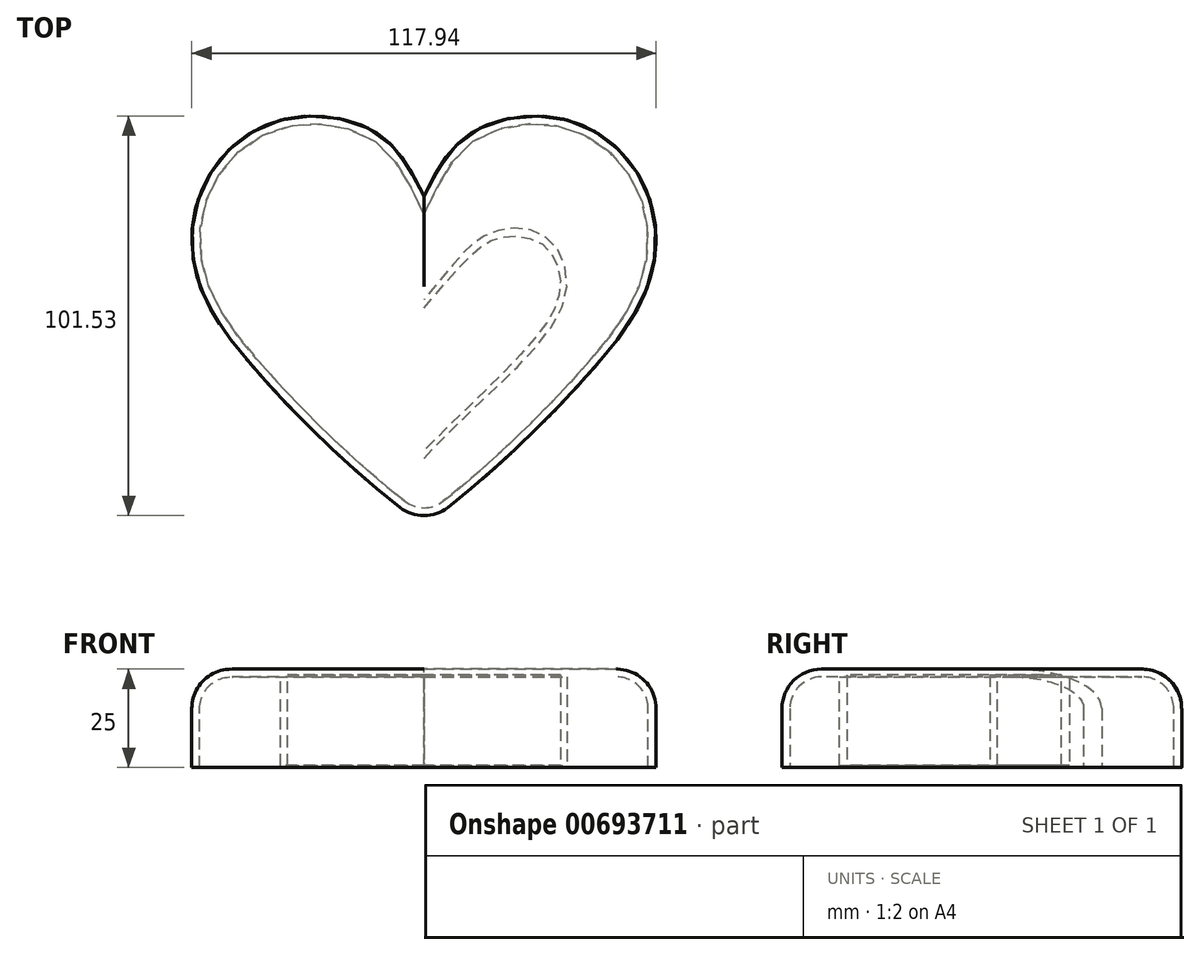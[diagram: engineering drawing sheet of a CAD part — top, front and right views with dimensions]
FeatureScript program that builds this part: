
annotation { "Feature Type Name" : "Feature", "Feature Type Description" : "" }
export const myFeature = defineFeature(function(context is Context, id is Id, definition is map)
    precondition{}
    {
        {
            var Q0;
            Q0=qCreatedBy(makeId("Top.planeOp"),FACE);
            var sketch = newSketch(context, id + "F0", { "sketchPlane" : qUnion([Q0])});
            skLineSegment(sketch, "E0", {"start": v(0, 39.92) * mm, "end": v(0, -43.63) * mm, "construction": true});
            skFitSpline(sketch, "E1", {"points": [v(0, 39.92) * mm, v(14.39, 57.24) * mm, v(36.67, 59.1) * mm, v(54, 46.1) * mm, v(58.95, 27.54) * mm, v(53.69, 10.21) * mm, v(41.3, -5.88) * mm, v(25.84, -21.97) * mm, v(0, -43.63) * mm], "startDerivative": vector(107.36, 222.12) * mm, "endDerivative": vector(-154.66, -101.42) * mm});
            skFitSpline(sketch, "E2.MirrorCS", {"points": [v(0, 39.92) * mm, v(-14.39, 57.24) * mm, v(-36.67, 59.1) * mm, v(-54, 46.1) * mm, v(-58.95, 27.54) * mm, v(-53.69, 10.21) * mm, v(-41.3, -5.88) * mm, v(-25.84, -21.97) * mm, v(0, -43.63) * mm], "startDerivative": vector(-107.36, 222.12) * mm, "endDerivative": vector(154.66, -101.42) * mm});
            skSolve(sketch);
        }
        {
            var Q0;
            Q0 = qSketchRegion(id + "F0", true);
            extrude(context, id + "F1", {"entities" : qUnion([Q0]), "depth" : 25 * mm, "offsetDistance" : 25 * mm});
        }
        {
            var Q0;
            Q0=makeQuery(id+"F1.opExtrude","CAP_EDGE",EDGE,{"disambiguationData":[OSD([sQuery(id+"F0.wireOp",EDGE,"E2.MirrorCS")])],"isStart":false});
            var Q1;
            Q1=makeQuery(id+"F1.opExtrude","CAP_EDGE",EDGE,{"disambiguationData":[OSD([sQuery(id+"F0.wireOp",EDGE,"E1")])],"isStart":false});
            var Q2;
            {var subQ0=sQuery(id+"F0.wireOp",EDGE,"E2.MirrorCS");var subQ1=sQuery(id+"F0.wireOp",EDGE,"E1");Q2=makeQuery(id+"F1.opExtrude","SWEPT_EDGE",EDGE,{"disambiguationData":[OSD([subQ1,subQ0]),TDD([makeQuery(id+"F0.imprint","INTERSECT",VERTEX,{"disambiguationData":[OD(1.0)],"derivedFrom":[subQ1,subQ0]})])]});}
            fillet(context, id + "F2", {"entities" : qUnion([Q0, Q1, Q2]), "radius" : 10 * mm, "tangentPropagation" : true, "allowEdgeOverflow" : false});
        }
        {
            var Q0;
            Q0=makeQuery(id+"F1.opExtrude","CAP_FACE",FACE,{"disambiguationData":[OSD([sQuery(id+"F0.wireOp",EDGE,"E1"),sQuery(id+"F0.wireOp",EDGE,"E2.MirrorCS")])],"isStart":true});
            shell(context, id + "F3", {"entities" : qUnion([Q0]), "thickness" : 2 * mm});
        }
        {
            var Q0;
            {var subQ0=sQuery(id+"F0.wireOp",EDGE,"E2.MirrorCS");var subQ1=sQuery(id+"F0.wireOp",EDGE,"E1");Q0=makeQuery(id+"F3.opShell","OFFSET_FACE",FACE,{"disambiguationData":[OSD([subQ1,subQ0]),TDD([makeQuery(id+"F1.opExtrude","CAP_FACE",FACE,{"disambiguationData":[OSD([subQ1,subQ0])],"isStart":false})])]});}
            var sketch = newSketch(context, id + "F4", { "sketchPlane" : qUnion([Q0])});
            skLineSegment(sketch, "E3", {"start": v(0, 26.76) * mm, "end": v(0, -13.46) * mm, "construction": true});
            skFitSpline(sketch, "E4", {"points": [v(0, 26.76) * mm, v(15.62, 11.29) * mm, v(36.04, -14.7) * mm, v(29.85, -30.17) * mm, v(16.24, -30.17) * mm, v(8.2, -23.37) * mm, v(0, -13.46) * mm], "startDerivative": vector(63.72, -68.45) * mm, "endDerivative": vector(-45.88, 60.47) * mm});
            skFitSpline(sketch, "E5.MirrorCS", {"points": [v(0, 26.76) * mm, v(-15.62, 11.29) * mm, v(-36.04, -14.7) * mm, v(-29.85, -30.17) * mm, v(-16.24, -30.17) * mm, v(-8.2, -23.37) * mm, v(0, -13.46) * mm], "startDerivative": vector(-63.72, -68.45) * mm, "endDerivative": vector(45.88, 60.47) * mm});
            skSolve(sketch);
        }
        {
            var Q0;
            Q0 = qSketchRegion(id + "F4", true);
            extrude(context, id + "F5", {"entities" : qUnion([Q0]), "operationType" : NewBodyOperationType.ADD, "depth" : 22.5 * mm, "offsetDistance" : 25 * mm});
        }
        {
            var Q0;
            Q0=makeQuery(id+"F5.opExtrude","CAP_FACE",FACE,{"disambiguationData":[OSD([sQuery(id+"F4.wireOp",EDGE,"E4"),sQuery(id+"F4.wireOp",EDGE,"E5.MirrorCS")])],"isStart":false});
            var sketch = newSketch(context, id + "F6", { "sketchPlane" : qUnion([Q0])});
            skLineSegment(sketch, "E6", {"start": v(0, -11.46) * mm, "end": v(0, 24.76) * mm, "construction": true});
            skFitSpline(sketch, "E7", {"points": [v(0, -11.46) * mm, v(11.97, -24.8) * mm, v(19.8, -29.39) * mm, v(30.28, -27.51) * mm, v(34.67, -17.48) * mm, v(28.56, -4.16) * mm, v(0, 24.76) * mm], "startDerivative": vector(66.3, -74.48) * mm, "endDerivative": vector(-120.95, 120.88) * mm});
            skFitSpline(sketch, "E8.MirrorCS", {"points": [v(0, -11.46) * mm, v(-11.97, -24.8) * mm, v(-19.8, -29.39) * mm, v(-30.28, -27.51) * mm, v(-34.67, -17.48) * mm, v(-28.56, -4.16) * mm, v(0, 24.76) * mm], "startDerivative": vector(-66.3, -74.48) * mm, "endDerivative": vector(120.95, 120.88) * mm});
            skSolve(sketch);
        }
        {
            var Q0;
            Q0 = qSketchRegion(id + "F6", true);
            extrude(context, id + "F7", {"entities" : qUnion([Q0]), "operationType" : NewBodyOperationType.REMOVE, "oppositeDirection" : true, "depth" : 23 * mm, "offsetDistance" : 25 * mm});
        }
    });
